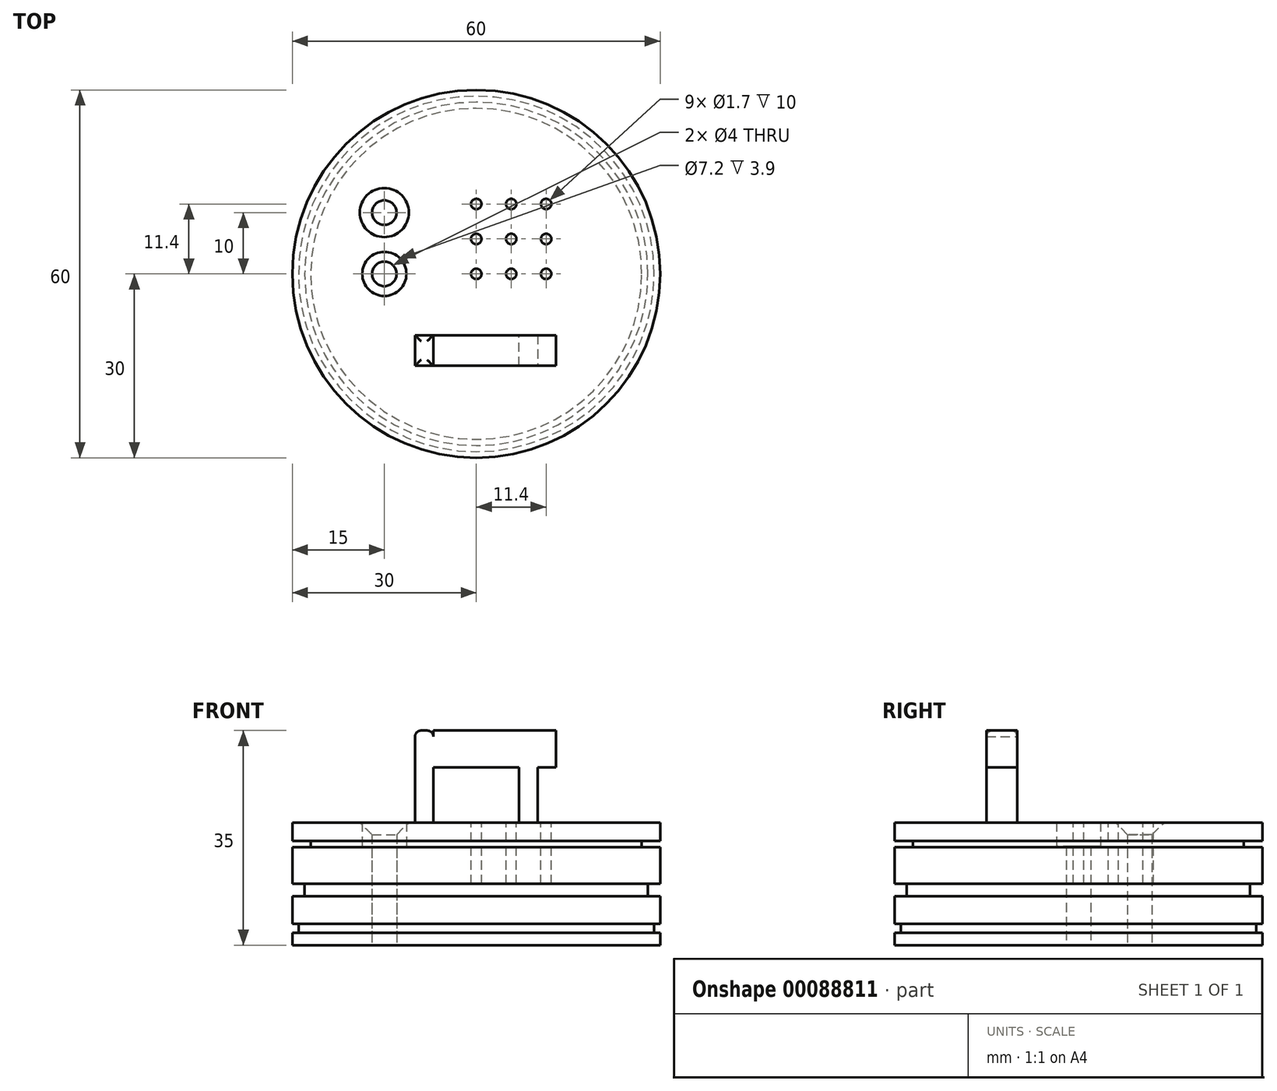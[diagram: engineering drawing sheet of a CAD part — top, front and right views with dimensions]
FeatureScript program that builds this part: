
annotation { "Feature Type Name" : "Feature", "Feature Type Description" : "" }
export const myFeature = defineFeature(function(context is Context, id is Id, definition is map)
    precondition{}
    {
        {
            var Q0;
            Q0=qCreatedBy(makeId("Front.planeOp"),FACE);
            var sketch = newSketch(context, id + "F0", { "sketchPlane" : qUnion([Q0])});
            skLineSegment(sketch, "E0", {"start": v(-30, 22.04) * mm, "end": v(0, 22.04) * mm});
            skLineSegment(sketch, "E1", {"start": v(0, 22.04) * mm, "end": v(0, 12.04) * mm});
            skLineSegment(sketch, "E2", {"start": v(-30, 22.04) * mm, "end": v(-30, 2.04) * mm});
            skLineSegment(sketch, "E3", {"start": v(-30, 2.04) * mm, "end": v(0, 2.04) * mm});
            skLineSegment(sketch, "E4", {"start": v(0, 12.04) * mm, "end": v(-2, 12.04) * mm});
            skLineSegment(sketch, "E5", {"start": v(-2, 12.04) * mm, "end": v(-2, 10.04) * mm});
            skLineSegment(sketch, "E6", {"start": v(-2, 10.04) * mm, "end": v(0, 10.04) * mm});
            skLineSegment(sketch, "E7.trimOffspring", {"start": v(0, 10.04) * mm, "end": v(0, 2.04) * mm});
            skLineSegment(sketch, "E8", {"start": v(0, 2.04) * mm, "end": v(0, 4.04) * mm});
            skLineSegment(sketch, "E9", {"start": v(0, 4.04) * mm, "end": v(-1, 4.04) * mm});
            skLineSegment(sketch, "E10", {"start": v(-1, 4.04) * mm, "end": v(-1, 5.54) * mm});
            skLineSegment(sketch, "E11", {"start": v(-1, 5.54) * mm, "end": v(0, 5.54) * mm});
            skLineSegment(sketch, "E12", {"start": v(0, 22.04) * mm, "end": v(0, 19.04) * mm});
            skLineSegment(sketch, "E13", {"start": v(0, 19.04) * mm, "end": v(-3, 19.04) * mm});
            skLineSegment(sketch, "E14", {"start": v(-3, 19.04) * mm, "end": v(-3, 18.04) * mm});
            skLineSegment(sketch, "E15", {"start": v(-3, 18.04) * mm, "end": v(0, 18.04) * mm});
            skSolve(sketch);
        }
        {
            var Q0;
            Q0=makeQuery(id+"F0.imprint","IMPRINT",FACE,{"disambiguationData":[TD([[makeQuery(id+"F0.imprint","IMPRINT",EDGE,{"derivedFrom":sQuery(id+"F0.wireOp",EDGE,"E0")}),-1.0]])]});
            var Q1;
            Q1=sQuery(id+"F0.wireOp",EDGE,"E2");
            revolve(context, id + "F1", {"entities" : qUnion([Q0]), "axis" : qUnion([Q1]), "revolveType" : RevolveType.FULL});
        }
        {
            var Q0;
            Q0=makeQuery(id+"F1.opRevolve","SWEPT_FACE",FACE,{"disambiguationData":[OSD([sQuery(id+"F0.wireOp",EDGE,"E0")])]});
            var sketch = newSketch(context, id + "F2", { "sketchPlane" : qUnion([Q0])});
            skCircle(sketch, "E16", {"center": v(-30, 0) * mm, "radius": 0.85 * mm});
            skCircle(sketch, "E17.0.1.0", {"center": v(-30, 5.7) * mm, "radius": 0.85 * mm});
            skCircle(sketch, "E17.0.2.0", {"center": v(-30, 11.4) * mm, "radius": 0.85 * mm});
            skCircle(sketch, "E17.1.0.0", {"center": v(-24.3, 0) * mm, "radius": 0.85 * mm});
            skCircle(sketch, "E17.1.1.0", {"center": v(-24.3, 5.7) * mm, "radius": 0.85 * mm});
            skCircle(sketch, "E17.1.2.0", {"center": v(-24.3, 11.4) * mm, "radius": 0.85 * mm});
            skCircle(sketch, "E17.2.0.0", {"center": v(-18.6, 0) * mm, "radius": 0.85 * mm});
            skCircle(sketch, "E17.2.1.0", {"center": v(-18.6, 5.7) * mm, "radius": 0.85 * mm});
            skCircle(sketch, "E17.2.2.0", {"center": v(-18.6, 11.4) * mm, "radius": 0.85 * mm});
            skLineSegment(sketch, "E17.direction1", {"start": v(-30, 0) * mm, "end": v(-24.3, 0) * mm, "construction": true});
            skLineSegment(sketch, "E17.direction2", {"start": v(-30, 0) * mm, "end": v(-30, 5.7) * mm, "construction": true});
            skLineSegment(sketch, "E18", {"start": v(-40, -10) * mm, "end": v(-40, -15) * mm});
            skLineSegment(sketch, "E19", {"start": v(-40, -15) * mm, "end": v(-37, -15) * mm});
            skLineSegment(sketch, "E20", {"start": v(-37, -15) * mm, "end": v(-37, -10) * mm});
            skLineSegment(sketch, "E21.MirrorCS", {"start": v(-23, -15) * mm, "end": v(-23, -10) * mm});
            skLineSegment(sketch, "E22.MirrorCS", {"start": v(-20, -10) * mm, "end": v(-20, -15) * mm});
            skLineSegment(sketch, "E23.MirrorCS", {"start": v(-20, -15) * mm, "end": v(-23, -15) * mm});
            skLineSegment(sketch, "E24", {"start": v(-40, -10) * mm, "end": v(-37, -10) * mm});
            skLineSegment(sketch, "E25", {"start": v(-23, -10) * mm, "end": v(-20, -10) * mm});
            skLineSegment(sketch, "E26", {"start": v(-30, 0) * mm, "end": v(-45, 0) * mm});
            skLineSegment(sketch, "E27", {"start": v(-45, 0) * mm, "end": v(-45, 10) * mm});
            skSolve(sketch);
        }
        {
            var Q0;
            Q0=makeQuery(id+"F2.imprint","IMPRINT",FACE,{"disambiguationData":[TD([[makeQuery(id+"F2.imprint","IMPRINT",EDGE,{"derivedFrom":sQuery(id+"F2.wireOp",EDGE,"E16")}),1.0]])]});
            var Q1;
            Q1=makeQuery(id+"F2.imprint","IMPRINT",FACE,{"disambiguationData":[TD([[makeQuery(id+"F2.imprint","IMPRINT",EDGE,{"derivedFrom":sQuery(id+"F2.wireOp",EDGE,"E17.0.1.0")}),1.0]])]});
            var Q2;
            Q2=makeQuery(id+"F2.imprint","IMPRINT",FACE,{"disambiguationData":[TD([[makeQuery(id+"F2.imprint","IMPRINT",EDGE,{"derivedFrom":sQuery(id+"F2.wireOp",EDGE,"E17.0.2.0")}),1.0]])]});
            var Q3;
            Q3=makeQuery(id+"F2.imprint","IMPRINT",FACE,{"disambiguationData":[TD([[makeQuery(id+"F2.imprint","IMPRINT",EDGE,{"derivedFrom":sQuery(id+"F2.wireOp",EDGE,"E17.1.0.0")}),1.0]])]});
            var Q4;
            Q4=makeQuery(id+"F2.imprint","IMPRINT",FACE,{"disambiguationData":[TD([[makeQuery(id+"F2.imprint","IMPRINT",EDGE,{"derivedFrom":sQuery(id+"F2.wireOp",EDGE,"E17.1.1.0")}),1.0]])]});
            var Q5;
            Q5=makeQuery(id+"F2.imprint","IMPRINT",FACE,{"disambiguationData":[TD([[makeQuery(id+"F2.imprint","IMPRINT",EDGE,{"derivedFrom":sQuery(id+"F2.wireOp",EDGE,"E17.1.2.0")}),1.0]])]});
            var Q6;
            Q6=makeQuery(id+"F2.imprint","IMPRINT",FACE,{"disambiguationData":[TD([[makeQuery(id+"F2.imprint","IMPRINT",EDGE,{"derivedFrom":sQuery(id+"F2.wireOp",EDGE,"E17.2.0.0")}),1.0]])]});
            var Q7;
            Q7=makeQuery(id+"F2.imprint","IMPRINT",FACE,{"disambiguationData":[TD([[makeQuery(id+"F2.imprint","IMPRINT",EDGE,{"derivedFrom":sQuery(id+"F2.wireOp",EDGE,"E17.2.1.0")}),1.0]])]});
            var Q8;
            Q8=makeQuery(id+"F2.imprint","IMPRINT",FACE,{"disambiguationData":[TD([[makeQuery(id+"F2.imprint","IMPRINT",EDGE,{"derivedFrom":sQuery(id+"F2.wireOp",EDGE,"E17.2.2.0")}),1.0]])]});
            extrude(context, id + "F3", {"entities" : qUnion([Q0, Q1, Q2, Q3, Q4, Q5, Q6, Q7, Q8]), "operationType" : NewBodyOperationType.REMOVE, "oppositeDirection" : true, "depth" : 10 * mm});
        }
        {
            var Q0;
            Q0=makeQuery(id+"F2.imprint","IMPRINT",FACE,{"disambiguationData":[TD([[makeQuery(id+"F2.imprint","IMPRINT",EDGE,{"derivedFrom":sQuery(id+"F2.wireOp",EDGE,"E21.MirrorCS")}),-1.0]])]});
            var Q1;
            Q1=makeQuery(id+"F2.imprint","IMPRINT",FACE,{"disambiguationData":[TD([[makeQuery(id+"F2.imprint","IMPRINT",EDGE,{"derivedFrom":sQuery(id+"F2.wireOp",EDGE,"E18")}),1.0]])]});
            extrude(context, id + "F4", {"entities" : qUnion([Q0, Q1]), "operationType" : NewBodyOperationType.ADD, "depth" : 15 * mm});
        }
        {
            var Q0;
            Q0=makeQuery(id+"F4.opExtrude","SWEPT_FACE",FACE,{"disambiguationData":[OSD([sQuery(id+"F2.wireOp",EDGE,"E20")])]});
            var sketch = newSketch(context, id + "F5", { "sketchPlane" : qUnion([Q0])});
            skLineSegment(sketch, "E28", {"start": v(-15, 37.04) * mm, "end": v(-10, 37.04) * mm});
            skLineSegment(sketch, "E29", {"start": v(-10, 37.04) * mm, "end": v(-10, 34.04) * mm});
            skLineSegment(sketch, "E30", {"start": v(-10, 34.04) * mm, "end": v(-15, 34.04) * mm});
            skLineSegment(sketch, "E31", {"start": v(-15, 34.04) * mm, "end": v(-15, 37.04) * mm});
            skLineSegment(sketch, "E32", {"start": v(-15, 34.04) * mm, "end": v(-15, 31.04) * mm});
            skLineSegment(sketch, "E33", {"start": v(-15, 31.04) * mm, "end": v(-10, 31.04) * mm});
            skLineSegment(sketch, "E34", {"start": v(-10, 31.04) * mm, "end": v(-10, 34.04) * mm});
            skSolve(sketch);
        }
        {
            var Q0;
            Q0=makeQuery(id+"F4.opExtrude","CAP_FACE",FACE,{"disambiguationData":[OSD([sQuery(id+"F2.wireOp",EDGE,"E18"),sQuery(id+"F2.wireOp",EDGE,"E19"),sQuery(id+"F2.wireOp",EDGE,"E20"),sQuery(id+"F2.wireOp",EDGE,"E24")])],"isStart":false});
            var Q1;
            Q1=makeQuery(id+"F4.opExtrude","CAP_FACE",FACE,{"disambiguationData":[OSD([sQuery(id+"F2.wireOp",EDGE,"E21.MirrorCS"),sQuery(id+"F2.wireOp",EDGE,"E22.MirrorCS"),sQuery(id+"F2.wireOp",EDGE,"E23.MirrorCS"),sQuery(id+"F2.wireOp",EDGE,"E25")])],"isStart":false});
            fillet(context, id + "F6", {"entities" : qUnion([Q0, Q1]), "radius" : 1 * mm, "tangentPropagation" : true, "allowEdgeOverflow" : false});
        }
        {
            var Q0;
            Q0=sQuery(id+"F2.wireOp",VERTEX,"E27.start");
            var Q1;
            Q1=makeQuery(id+"F1.opRevolve","SWEPT_BODY",BODY,{"disambiguationData":[OSD([sQuery(id+"F0.wireOp",EDGE,"E0"),sQuery(id+"F0.wireOp",EDGE,"E1"),sQuery(id+"F0.wireOp",EDGE,"E2"),sQuery(id+"F0.wireOp",EDGE,"E3"),sQuery(id+"F0.wireOp",EDGE,"E4"),sQuery(id+"F0.wireOp",EDGE,"E5"),sQuery(id+"F0.wireOp",EDGE,"E6"),sQuery(id+"F0.wireOp",EDGE,"E7.trimOffspring"),sQuery(id+"F0.wireOp",EDGE,"E8"),sQuery(id+"F0.wireOp",EDGE,"E9"),sQuery(id+"F0.wireOp",EDGE,"E10"),sQuery(id+"F0.wireOp",EDGE,"E11"),sQuery(id+"F0.wireOp",EDGE,"E12"),sQuery(id+"F0.wireOp",EDGE,"E13"),sQuery(id+"F0.wireOp",EDGE,"E14"),sQuery(id+"F0.wireOp",EDGE,"E15")])]});
            hole(context, id + "F7", {"style" : HoleStyle.C_BORE, "endStyle" : HoleEndStyle.THROUGH, "holeDiameter" : 4 * mm, "cBoreDiameter" : 7.2 * mm, "cBoreDepth" : 3.9 * mm, "locations" : qUnion([Q0]), "scope" : qUnion([Q1]), "isTappedThrough" : true, "startStyle" : HoleStartStyle.PART});
        }
        {
            var Q0;
            Q0=sQuery(id+"F2.wireOp",VERTEX,"E27.end");
            var Q1;
            Q1=makeQuery(id+"F1.opRevolve","SWEPT_BODY",BODY,{"disambiguationData":[OSD([sQuery(id+"F0.wireOp",EDGE,"E0"),sQuery(id+"F0.wireOp",EDGE,"E1"),sQuery(id+"F0.wireOp",EDGE,"E2"),sQuery(id+"F0.wireOp",EDGE,"E3"),sQuery(id+"F0.wireOp",EDGE,"E4"),sQuery(id+"F0.wireOp",EDGE,"E5"),sQuery(id+"F0.wireOp",EDGE,"E6"),sQuery(id+"F0.wireOp",EDGE,"E7.trimOffspring"),sQuery(id+"F0.wireOp",EDGE,"E8"),sQuery(id+"F0.wireOp",EDGE,"E9"),sQuery(id+"F0.wireOp",EDGE,"E10"),sQuery(id+"F0.wireOp",EDGE,"E11"),sQuery(id+"F0.wireOp",EDGE,"E12"),sQuery(id+"F0.wireOp",EDGE,"E13"),sQuery(id+"F0.wireOp",EDGE,"E14"),sQuery(id+"F0.wireOp",EDGE,"E15")])]});
            hole(context, id + "F8", {"style" : HoleStyle.C_SINK, "endStyle" : HoleEndStyle.BLIND, "holeDiameter" : 4 * mm, "cSinkDiameter" : 8 * mm, "cSinkAngle" : 90 * degree, "holeDepth" : 20 * mm, "locations" : qUnion([Q0]), "scope" : qUnion([Q1]), "startStyle" : HoleStartStyle.PART});
        }
        {
            var Q0;
            Q0=makeQuery(id+"F5.imprint","IMPRINT",FACE,{"disambiguationData":[TD([[makeQuery(id+"F5.imprint","IMPRINT",EDGE,{"derivedFrom":sQuery(id+"F5.wireOp",EDGE,"E30")}),1.0]])]});
            extrude(context, id + "F9", {"entities" : qUnion([Q0]), "operationType" : NewBodyOperationType.ADD, "depth" : 14 * mm});
        }
        {
            var Q0;
            Q0 = qSketchRegion(id + "F5", true);
            extrude(context, id + "F10", {"entities" : qUnion([Q0]), "operationType" : NewBodyOperationType.ADD, "depth" : 20 * mm});
        }
    });
